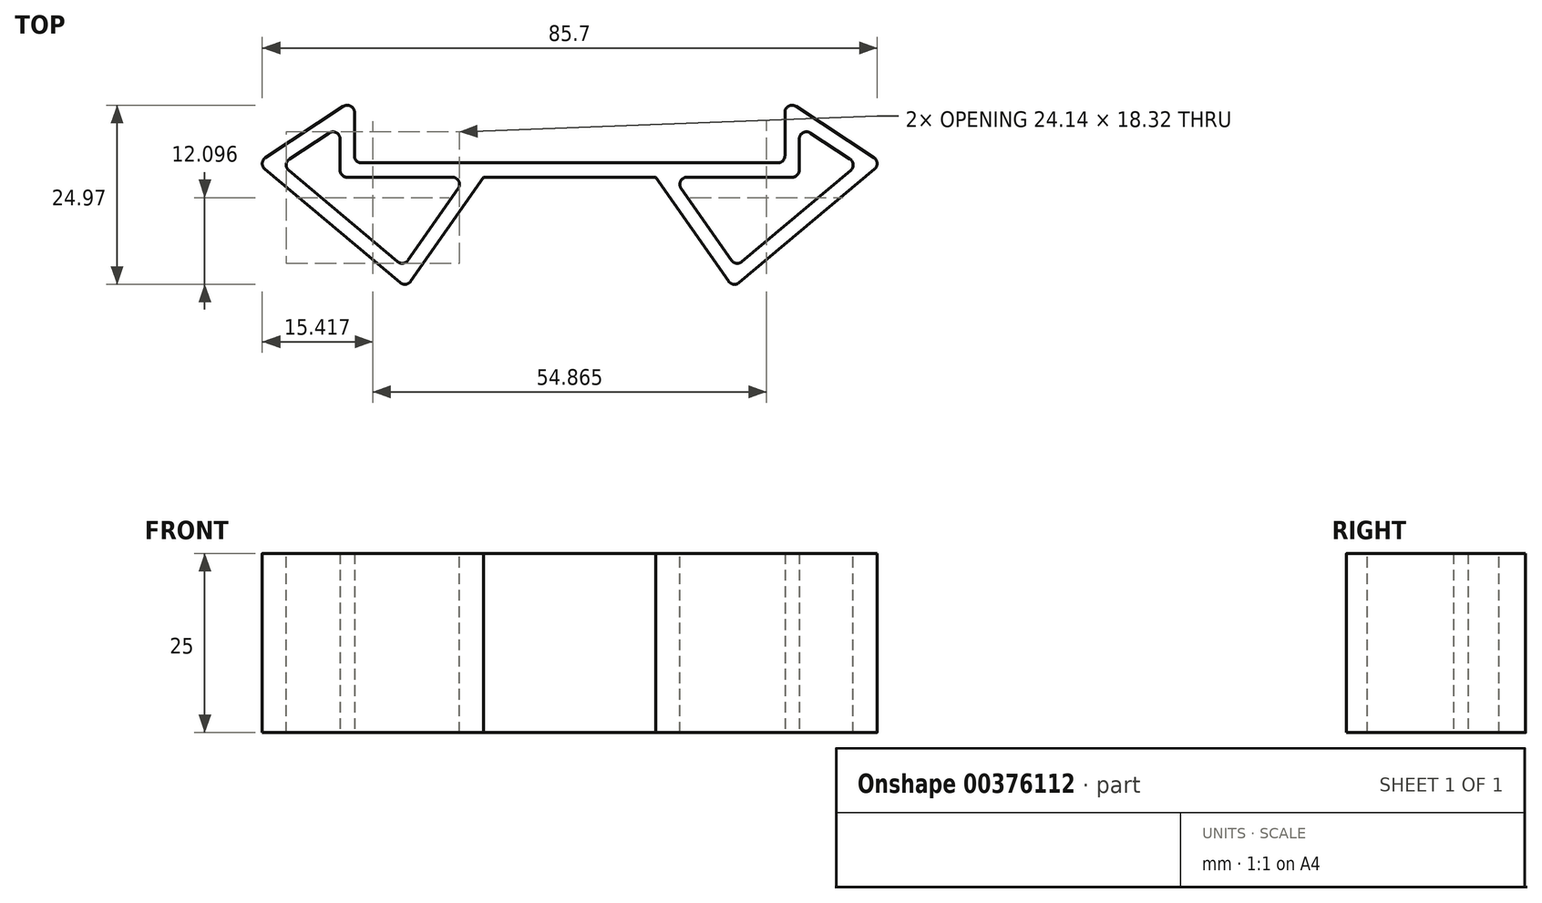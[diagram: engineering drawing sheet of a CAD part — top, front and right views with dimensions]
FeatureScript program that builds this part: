
annotation { "Feature Type Name" : "Feature", "Feature Type Description" : "" }
export const myFeature = defineFeature(function(context is Context, id is Id, definition is map)
    precondition{}
    {
        {
            var Q0;
            Q0=qCreatedBy(makeId("Top.planeOp"),FACE);
            var sketch = newSketch(context, id + "F0", { "sketchPlane" : qUnion([Q0])});
            skLineSegment(sketch, "E0", {"start": v(0, 0) * mm, "end": v(-30, 0) * mm});
            skLineSegment(sketch, "E1", {"start": v(-30, 0) * mm, "end": v(-30, 8.9) * mm});
            skLineSegment(sketch, "E2", {"start": v(-30, 8.9) * mm, "end": v(-43.52, 0) * mm});
            skLineSegment(sketch, "E3", {"start": v(-43.52, 0) * mm, "end": v(-22.78, -17.4) * mm});
            skLineSegment(sketch, "E4", {"start": v(-22.78, -17.4) * mm, "end": v(-12, -2) * mm});
            skLineSegment(sketch, "E5", {"start": v(-12, -2) * mm, "end": v(0, -2) * mm});
            skLineSegment(sketch, "E6", {"start": v(0, 14.81) * mm, "end": v(0, -16.78) * mm});
            skLineSegment(sketch, "E7.0", {"start": v(-40.17, -0.2) * mm, "end": v(-23.17, -14.46) * mm});
            skLineSegment(sketch, "E7.1", {"start": v(-29.77, 6.65) * mm, "end": v(-40.17, -0.2) * mm});
            skLineSegment(sketch, "E8.0", {"start": v(-32, -2) * mm, "end": v(-32, 9.4) * mm});
            skLineSegment(sketch, "E8.1", {"start": v(0, -2) * mm, "end": v(-32, -2) * mm});
            skLineSegment(sketch, "E9.0", {"start": v(-23.17, -14.46) * mm, "end": v(-14.44, -2) * mm});
            skLineSegment(sketch, "E10.MirrorCS", {"start": v(30, 0) * mm, "end": v(30, 8.9) * mm});
            skLineSegment(sketch, "E11.MirrorCS", {"start": v(30, 8.9) * mm, "end": v(43.52, 0) * mm});
            skLineSegment(sketch, "E12.MirrorCS", {"start": v(43.52, 0) * mm, "end": v(22.78, -17.4) * mm});
            skLineSegment(sketch, "E13.MirrorCS", {"start": v(22.78, -17.4) * mm, "end": v(12, -2) * mm});
            skLineSegment(sketch, "E14.MirrorCS", {"start": v(23.17, -14.46) * mm, "end": v(14.44, -2) * mm});
            skLineSegment(sketch, "E15.MirrorCS", {"start": v(32, -2) * mm, "end": v(32, 9.4) * mm});
            skLineSegment(sketch, "E16.MirrorCS", {"start": v(29.77, 6.65) * mm, "end": v(40.17, -0.2) * mm});
            skLineSegment(sketch, "E17.MirrorCS", {"start": v(40.17, -0.2) * mm, "end": v(23.17, -14.46) * mm});
            skLineSegment(sketch, "E18.MirrorCS", {"start": v(0, -2) * mm, "end": v(32, -2) * mm});
            skLineSegment(sketch, "E19.MirrorCS", {"start": v(12, -2) * mm, "end": v(0, -2) * mm});
            skLineSegment(sketch, "E20.MirrorCS", {"start": v(0, 0) * mm, "end": v(30, 0) * mm});
            skPoint(sketch, "E21", {"position": v(-16, -2) * mm});
            skSolve(sketch);
        }
        {
            var Q0;
            {var subQ6=sQuery(id+"F0.wireOp",EDGE,"E3");Q0=makeQuery(id+"F0.imprint","IMPRINT",FACE,{"disambiguationData":[TD([[makeQuery(id+"F0.imprint","IMPRINT",EDGE,{"derivedFrom":subQ6}),1.0]])]});}
            var Q1;
            {var subQ0=sQuery(id+"F0.wireOp",EDGE,"E2");var subQ1=sQuery(id+"F0.wireOp",EDGE,"E1");var subQ2=makeQuery(id+"F0.imprint","INTERSECT",VERTEX,{"derivedFrom":[subQ1,subQ0]});Q1=makeQuery(id+"F0.imprint","IMPRINT",FACE,{"disambiguationData":[TD([[makeQuery(id+"F0.imprint","IMPRINT",EDGE,{"disambiguationData":[TD([[subQ2,1.0]])],"derivedFrom":subQ1}),1.0]])]});}
            var Q2;
            {var subQ1=sQuery(id+"F0.wireOp",EDGE,"E0");Q2=makeQuery(id+"F0.imprint","IMPRINT",FACE,{"disambiguationData":[TD([[makeQuery(id+"F0.imprint","IMPRINT",EDGE,{"derivedFrom":subQ1}),1.0]])]});}
            var Q3;
            {var subQ0=sQuery(id+"F0.wireOp",EDGE,"E12.MirrorCS");Q3=makeQuery(id+"F0.imprint","IMPRINT",FACE,{"disambiguationData":[TD([[makeQuery(id+"F0.imprint","IMPRINT",EDGE,{"derivedFrom":subQ0}),-1.0]])]});}
            var Q4;
            {var subQ7=sQuery(id+"F0.wireOp",EDGE,"E20.MirrorCS");Q4=makeQuery(id+"F0.imprint","IMPRINT",FACE,{"disambiguationData":[TD([[makeQuery(id+"F0.imprint","IMPRINT",EDGE,{"derivedFrom":subQ7}),-1.0]])]});}
            var Q5;
            {var subQ0=sQuery(id+"F0.wireOp",EDGE,"E11.MirrorCS");var subQ1=sQuery(id+"F0.wireOp",EDGE,"E10.MirrorCS");var subQ2=makeQuery(id+"F0.imprint","INTERSECT",VERTEX,{"derivedFrom":[subQ1,subQ0]});Q5=makeQuery(id+"F0.imprint","IMPRINT",FACE,{"disambiguationData":[TD([[makeQuery(id+"F0.imprint","IMPRINT",EDGE,{"disambiguationData":[TD([[subQ2,1.0]])],"derivedFrom":subQ1}),-1.0]])]});}
            extrude(context, id + "F1", {"entities" : qUnion([Q0, Q1, Q2, Q3, Q4, Q5]), "depth" : 25 * mm});
        }
        {
            var Q0;
            Q0=makeQuery(id+"F1.opExtrude","SWEPT_EDGE",EDGE,{"disambiguationData":[OSD([sQuery(id+"F0.wireOp",EDGE,"E1"),sQuery(id+"F0.wireOp",EDGE,"E2")])]});
            var Q1;
            Q1=makeQuery(id+"F1.opExtrude","SWEPT_EDGE",EDGE,{"disambiguationData":[OSD([sQuery(id+"F0.wireOp",EDGE,"E2"),sQuery(id+"F0.wireOp",EDGE,"E3")])]});
            var Q2;
            Q2=makeQuery(id+"F1.opExtrude","SWEPT_EDGE",EDGE,{"disambiguationData":[OSD([sQuery(id+"F0.wireOp",EDGE,"E3"),sQuery(id+"F0.wireOp",EDGE,"E4")])]});
            var Q3;
            Q3=makeQuery(id+"F1.opExtrude","SWEPT_EDGE",EDGE,{"disambiguationData":[OSD([sQuery(id+"F0.wireOp",EDGE,"E0"),sQuery(id+"F0.wireOp",EDGE,"E1")])]});
            var Q4;
            Q4=makeQuery(id+"F1.opExtrude","SWEPT_EDGE",EDGE,{"disambiguationData":[OSD([sQuery(id+"F0.wireOp",EDGE,"E8.0"),sQuery(id+"F0.wireOp",EDGE,"E8.1")])]});
            var Q5;
            Q5=makeQuery(id+"F1.opExtrude","SWEPT_EDGE",EDGE,{"disambiguationData":[OSD([sQuery(id+"F0.wireOp",EDGE,"E10.MirrorCS"),sQuery(id+"F0.wireOp",EDGE,"E20.MirrorCS")])]});
            var Q6;
            Q6=makeQuery(id+"F1.opExtrude","SWEPT_EDGE",EDGE,{"disambiguationData":[OSD([sQuery(id+"F0.wireOp",EDGE,"E10.MirrorCS"),sQuery(id+"F0.wireOp",EDGE,"E11.MirrorCS")])]});
            var Q7;
            Q7=makeQuery(id+"F1.opExtrude","SWEPT_EDGE",EDGE,{"disambiguationData":[OSD([sQuery(id+"F0.wireOp",EDGE,"E11.MirrorCS"),sQuery(id+"F0.wireOp",EDGE,"E12.MirrorCS")])]});
            var Q8;
            Q8=makeQuery(id+"F1.opExtrude","SWEPT_EDGE",EDGE,{"disambiguationData":[OSD([sQuery(id+"F0.wireOp",EDGE,"E15.MirrorCS"),sQuery(id+"F0.wireOp",EDGE,"E18.MirrorCS")])]});
            var Q9;
            Q9=makeQuery(id+"F1.opExtrude","SWEPT_EDGE",EDGE,{"disambiguationData":[OSD([sQuery(id+"F0.wireOp",EDGE,"E12.MirrorCS"),sQuery(id+"F0.wireOp",EDGE,"E13.MirrorCS")])]});
            var Q10;
            Q10=makeQuery(id+"F1.opExtrude","SWEPT_EDGE",EDGE,{"disambiguationData":[OSD([sQuery(id+"F0.wireOp",EDGE,"E14.MirrorCS"),sQuery(id+"F0.wireOp",EDGE,"E17.MirrorCS")])]});
            var Q11;
            Q11=makeQuery(id+"F1.opExtrude","SWEPT_EDGE",EDGE,{"disambiguationData":[OSD([sQuery(id+"F0.wireOp",EDGE,"E14.MirrorCS"),sQuery(id+"F0.wireOp",EDGE,"E18.MirrorCS")])]});
            var Q12;
            Q12=makeQuery(id+"F1.opExtrude","SWEPT_EDGE",EDGE,{"disambiguationData":[OSD([sQuery(id+"F0.wireOp",EDGE,"E15.MirrorCS"),sQuery(id+"F0.wireOp",EDGE,"E16.MirrorCS")])]});
            var Q13;
            Q13=makeQuery(id+"F1.opExtrude","SWEPT_EDGE",EDGE,{"disambiguationData":[OSD([sQuery(id+"F0.wireOp",EDGE,"E16.MirrorCS"),sQuery(id+"F0.wireOp",EDGE,"E17.MirrorCS")])]});
            var Q14;
            Q14=makeQuery(id+"F1.opExtrude","SWEPT_EDGE",EDGE,{"disambiguationData":[OSD([sQuery(id+"F0.wireOp",EDGE,"E7.0"),sQuery(id+"F0.wireOp",EDGE,"E7.1")])]});
            var Q15;
            Q15=makeQuery(id+"F1.opExtrude","SWEPT_EDGE",EDGE,{"disambiguationData":[OSD([sQuery(id+"F0.wireOp",EDGE,"E7.1"),sQuery(id+"F0.wireOp",EDGE,"E8.0")])]});
            var Q16;
            Q16=makeQuery(id+"F1.opExtrude","SWEPT_EDGE",EDGE,{"disambiguationData":[OSD([sQuery(id+"F0.wireOp",EDGE,"E7.0"),sQuery(id+"F0.wireOp",EDGE,"E9.0")])]});
            var Q17;
            Q17=makeQuery(id+"F1.opExtrude","SWEPT_EDGE",EDGE,{"disambiguationData":[OSD([sQuery(id+"F0.wireOp",EDGE,"E8.1"),sQuery(id+"F0.wireOp",EDGE,"E9.0")])]});
            fillet(context, id + "F2", {"entities" : qUnion([Q0, Q1, Q2, Q3, Q4, Q5, Q6, Q7, Q8, Q9, Q10, Q11, Q12, Q13, Q14, Q15, Q16, Q17]), "radius" : 1 * mm, "tangentPropagation" : true, "allowEdgeOverflow" : false});
        }
    });
